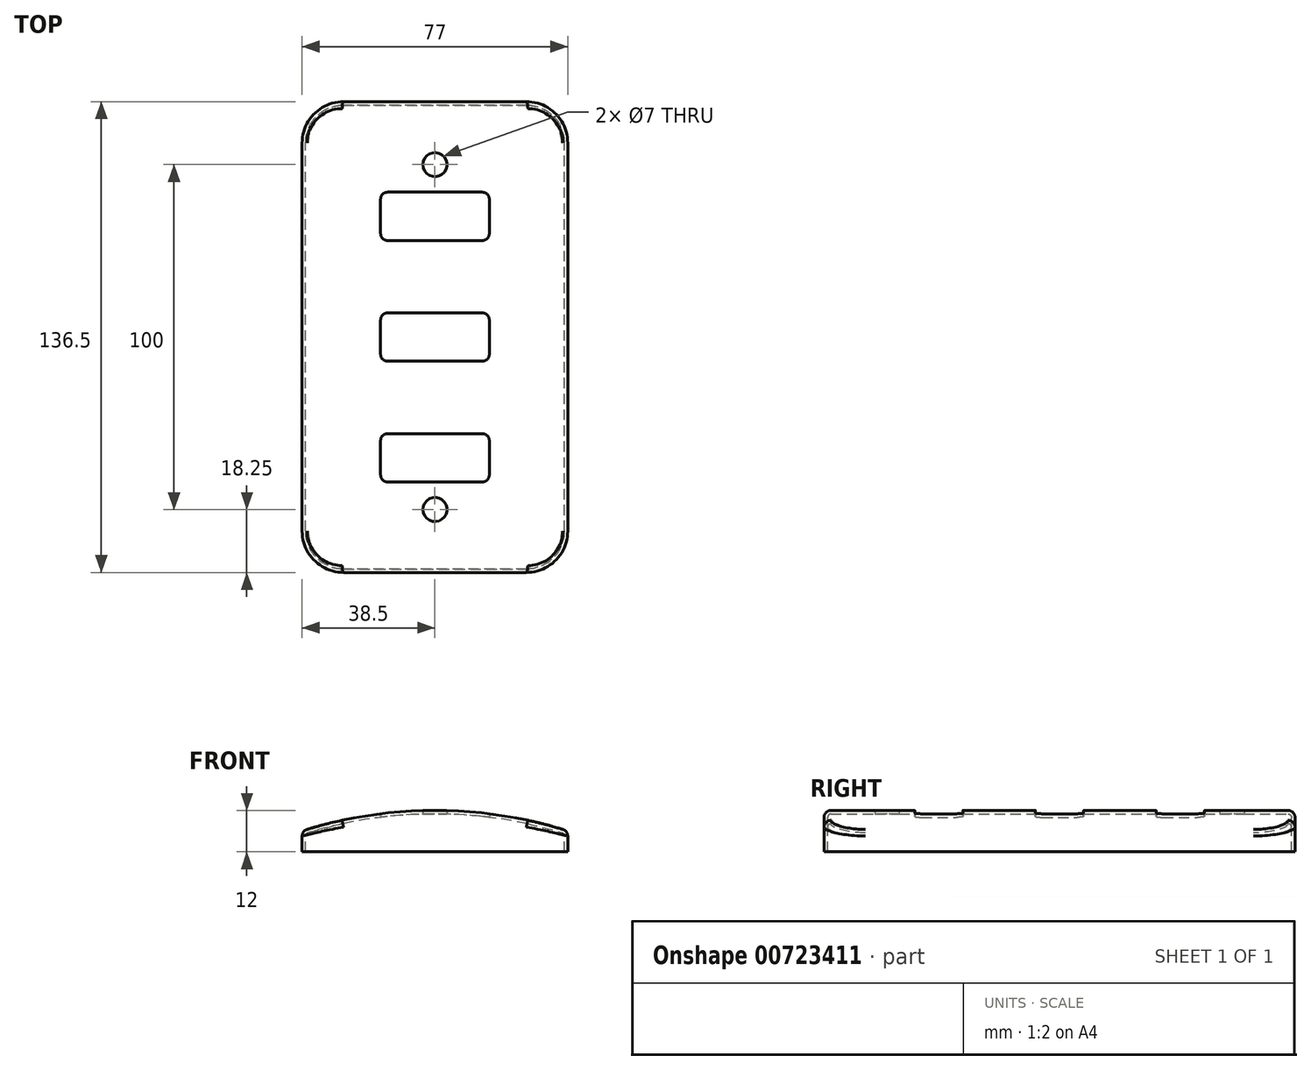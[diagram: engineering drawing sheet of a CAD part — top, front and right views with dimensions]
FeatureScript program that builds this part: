
annotation { "Feature Type Name" : "Feature", "Feature Type Description" : "" }
export const myFeature = defineFeature(function(context is Context, id is Id, definition is map)
    precondition{}
    {
        {
            var Q0;
            Q0=qCreatedBy(makeId("Front.planeOp"),FACE);
            var sketch = newSketch(context, id + "F0", { "sketchPlane" : qUnion([Q0])});
            skLineSegment(sketch, "E0.bottom", {"start": v(-38.5, 0) * mm, "end": v(38.5, 0) * mm});
            skLineSegment(sketch, "E0.left", {"start": v(-38.5, 0) * mm, "end": v(-38.5, 6.07) * mm});
            skLineSegment(sketch, "E0.right", {"start": v(38.5, 0) * mm, "end": v(38.5, 6.07) * mm});
            skArc(sketch, "E1", {"start": v(38.5, 6.07) * mm, "mid": v(0, 12) * mm, "end": v(-38.5, 6.07) * mm});
            skLineSegment(sketch, "E2", {"start": v(0, 0) * mm, "end": v(0, 12) * mm, "construction": true});
            skSolve(sketch);
        }
        {
            var Q0;
            Q0=makeQuery(id+"F0.imprint","IMPRINT",FACE,{"disambiguationData":[TD([[makeQuery(id+"F0.imprint","IMPRINT",EDGE,{"derivedFrom":sQuery(id+"F0.wireOp",EDGE,"E0.bottom")}),1.0]])]});
            extrude(context, id + "F1", {"entities" : qUnion([Q0]), "depth" : 136.5 * mm, "offsetDistance" : 25 * mm});
        }
        {
            var Q0;
            Q0=makeQuery(id+"F1.opExtrude","CAP_EDGE",EDGE,{"disambiguationData":[OSD([sQuery(id+"F0.wireOp",EDGE,"E0.right")])],"isStart":false});
            var Q1;
            Q1=makeQuery(id+"F1.opExtrude","CAP_EDGE",EDGE,{"disambiguationData":[OSD([sQuery(id+"F0.wireOp",EDGE,"E0.left")])],"isStart":false});
            var Q2;
            Q2=makeQuery(id+"F1.opExtrude","CAP_EDGE",EDGE,{"disambiguationData":[OSD([sQuery(id+"F0.wireOp",EDGE,"E0.right")])],"isStart":true});
            var Q3;
            Q3=makeQuery(id+"F1.opExtrude","CAP_EDGE",EDGE,{"disambiguationData":[OSD([sQuery(id+"F0.wireOp",EDGE,"E0.left")])],"isStart":true});
            fillet(context, id + "F2", {"entities" : qUnion([Q0, Q1, Q2, Q3]), "radius" : 12 * mm, "tangentPropagation" : true, "allowEdgeOverflow" : false});
        }
        {
            var Q0;
            Q0=makeQuery(id+"F1.opExtrude","SWEPT_FACE",FACE,{"disambiguationData":[OSD([sQuery(id+"F0.wireOp",EDGE,"E1")])]});
            fillet(context, id + "F3", {"entities" : qUnion([Q0]), "radius" : 2 * mm, "tangentPropagation" : true, "allowEdgeOverflow" : false});
        }
        {
            var Q0;
            Q0=makeQuery(id+"F1.opExtrude","SWEPT_FACE",FACE,{"disambiguationData":[OSD([sQuery(id+"F0.wireOp",EDGE,"E0.bottom")])]});
            shell(context, id + "F4", {"entities" : qUnion([Q0]), "thickness" : 1.02 * mm});
        }
        {
            var Q0;
            Q0=qCreatedBy(makeId("Top.planeOp"),FACE);
            var sketch = newSketch(context, id + "F5", { "sketchPlane" : qUnion([Q0])});
            skCircle(sketch, "E3", {"center": v(0, -18.25) * mm, "radius": 3.5 * mm});
            skCircle(sketch, "E4", {"center": v(0, -118.25) * mm, "radius": 3.5 * mm});
            skLineSegment(sketch, "E5.bottom", {"start": v(-15.75, -40.25) * mm, "end": v(15.75, -40.25) * mm});
            skLineSegment(sketch, "E5.top", {"start": v(-15.75, -26.25) * mm, "end": v(15.75, -26.25) * mm});
            skLineSegment(sketch, "E5.left", {"start": v(-15.75, -40.25) * mm, "end": v(-15.75, -26.25) * mm});
            skLineSegment(sketch, "E5.right", {"start": v(15.75, -40.25) * mm, "end": v(15.75, -26.25) * mm});
            skPoint(sketch, "E5.middle", {"position": v(0, -33.25) * mm});
            skLineSegment(sketch, "E6.bottom", {"start": v(-15.75, -75.25) * mm, "end": v(15.75, -75.25) * mm});
            skLineSegment(sketch, "E6.top", {"start": v(-15.75, -61.25) * mm, "end": v(15.75, -61.25) * mm});
            skLineSegment(sketch, "E6.left", {"start": v(-15.75, -75.25) * mm, "end": v(-15.75, -61.25) * mm});
            skLineSegment(sketch, "E6.right", {"start": v(15.75, -75.25) * mm, "end": v(15.75, -61.25) * mm});
            skPoint(sketch, "E6.middle", {"position": v(0, -68.25) * mm});
            skLineSegment(sketch, "E7.bottom", {"start": v(-15.75, -110.25) * mm, "end": v(15.75, -110.25) * mm});
            skLineSegment(sketch, "E7.top", {"start": v(-15.75, -96.25) * mm, "end": v(15.75, -96.25) * mm});
            skLineSegment(sketch, "E7.left", {"start": v(-15.75, -110.25) * mm, "end": v(-15.75, -96.25) * mm});
            skLineSegment(sketch, "E7.right", {"start": v(15.75, -110.25) * mm, "end": v(15.75, -96.25) * mm});
            skPoint(sketch, "E7.middle", {"position": v(0, -103.25) * mm});
            skPoint(sketch, "E8.0", {"position": v(38.5, -68.25) * mm});
            skSolve(sketch);
        }
        {
            var Q0;
            Q0=makeQuery(id+"F5.imprint","IMPRINT",FACE,{"disambiguationData":[TD([[makeQuery(id+"F5.imprint","IMPRINT",EDGE,{"derivedFrom":sQuery(id+"F5.wireOp",EDGE,"E4")}),1.0]])]});
            var Q1;
            Q1=makeQuery(id+"F5.imprint","IMPRINT",FACE,{"disambiguationData":[TD([[makeQuery(id+"F5.imprint","IMPRINT",EDGE,{"derivedFrom":sQuery(id+"F5.wireOp",EDGE,"E7.bottom")}),1.0]])]});
            var Q2;
            Q2=makeQuery(id+"F5.imprint","IMPRINT",FACE,{"disambiguationData":[TD([[makeQuery(id+"F5.imprint","IMPRINT",EDGE,{"derivedFrom":sQuery(id+"F5.wireOp",EDGE,"E6.bottom")}),1.0]])]});
            var Q3;
            Q3=makeQuery(id+"F5.imprint","IMPRINT",FACE,{"disambiguationData":[TD([[makeQuery(id+"F5.imprint","IMPRINT",EDGE,{"derivedFrom":sQuery(id+"F5.wireOp",EDGE,"E5.bottom")}),1.0]])]});
            var Q4;
            Q4=makeQuery(id+"F5.imprint","IMPRINT",FACE,{"disambiguationData":[TD([[makeQuery(id+"F5.imprint","IMPRINT",EDGE,{"derivedFrom":sQuery(id+"F5.wireOp",EDGE,"E3")}),1.0]])]});
            extrude(context, id + "F6", {"entities" : qUnion([Q0, Q1, Q2, Q3, Q4]), "operationType" : NewBodyOperationType.REMOVE, "endBound" : BoundingType.THROUGH_ALL, "depth" : 25 * mm, "offsetDistance" : 25 * mm});
        }
        {
            var Q0;
            Q0=makeQuery(id+"F6.boolean.opBoolean","COPY",EDGE,{"derivedFrom":makeQuery(id+"F6.opExtrude","SWEPT_EDGE",EDGE,{"disambiguationData":[OSD([sQuery(id+"F5.wireOp",EDGE,"E5.top"),sQuery(id+"F5.wireOp",EDGE,"E5.left")])]})});
            var Q1;
            Q1=makeQuery(id+"F6.boolean.opBoolean","COPY",EDGE,{"derivedFrom":makeQuery(id+"F6.opExtrude","SWEPT_EDGE",EDGE,{"disambiguationData":[OSD([sQuery(id+"F5.wireOp",EDGE,"E5.top"),sQuery(id+"F5.wireOp",EDGE,"E5.right")])]})});
            var Q2;
            Q2=makeQuery(id+"F6.boolean.opBoolean","COPY",EDGE,{"derivedFrom":makeQuery(id+"F6.opExtrude","SWEPT_EDGE",EDGE,{"disambiguationData":[OSD([sQuery(id+"F5.wireOp",EDGE,"E5.bottom"),sQuery(id+"F5.wireOp",EDGE,"E5.left")])]})});
            var Q3;
            Q3=makeQuery(id+"F6.boolean.opBoolean","COPY",EDGE,{"derivedFrom":makeQuery(id+"F6.opExtrude","SWEPT_EDGE",EDGE,{"disambiguationData":[OSD([sQuery(id+"F5.wireOp",EDGE,"E5.bottom"),sQuery(id+"F5.wireOp",EDGE,"E5.right")])]})});
            var Q4;
            Q4=makeQuery(id+"F6.boolean.opBoolean","COPY",EDGE,{"derivedFrom":makeQuery(id+"F6.opExtrude","SWEPT_EDGE",EDGE,{"disambiguationData":[OSD([sQuery(id+"F5.wireOp",EDGE,"E6.bottom"),sQuery(id+"F5.wireOp",EDGE,"E6.right")])]})});
            var Q5;
            Q5=makeQuery(id+"F6.boolean.opBoolean","COPY",EDGE,{"derivedFrom":makeQuery(id+"F6.opExtrude","SWEPT_EDGE",EDGE,{"disambiguationData":[OSD([sQuery(id+"F5.wireOp",EDGE,"E7.bottom"),sQuery(id+"F5.wireOp",EDGE,"E7.right")])]})});
            var Q6;
            Q6=makeQuery(id+"F6.boolean.opBoolean","COPY",EDGE,{"derivedFrom":makeQuery(id+"F6.opExtrude","SWEPT_EDGE",EDGE,{"disambiguationData":[OSD([sQuery(id+"F5.wireOp",EDGE,"E7.bottom"),sQuery(id+"F5.wireOp",EDGE,"E7.left")])]})});
            var Q7;
            Q7=makeQuery(id+"F6.boolean.opBoolean","COPY",EDGE,{"derivedFrom":makeQuery(id+"F6.opExtrude","SWEPT_EDGE",EDGE,{"disambiguationData":[OSD([sQuery(id+"F5.wireOp",EDGE,"E6.bottom"),sQuery(id+"F5.wireOp",EDGE,"E6.left")])]})});
            var Q8;
            Q8=makeQuery(id+"F6.boolean.opBoolean","COPY",EDGE,{"derivedFrom":makeQuery(id+"F6.opExtrude","SWEPT_EDGE",EDGE,{"disambiguationData":[OSD([sQuery(id+"F5.wireOp",EDGE,"E6.top"),sQuery(id+"F5.wireOp",EDGE,"E6.left")])]})});
            var Q9;
            Q9=makeQuery(id+"F6.boolean.opBoolean","COPY",EDGE,{"derivedFrom":makeQuery(id+"F6.opExtrude","SWEPT_EDGE",EDGE,{"disambiguationData":[OSD([sQuery(id+"F5.wireOp",EDGE,"E7.top"),sQuery(id+"F5.wireOp",EDGE,"E7.left")])]})});
            var Q10;
            Q10=makeQuery(id+"F6.boolean.opBoolean","COPY",EDGE,{"derivedFrom":makeQuery(id+"F6.opExtrude","SWEPT_EDGE",EDGE,{"disambiguationData":[OSD([sQuery(id+"F5.wireOp",EDGE,"E6.top"),sQuery(id+"F5.wireOp",EDGE,"E6.right")])]})});
            var Q11;
            Q11=makeQuery(id+"F6.boolean.opBoolean","COPY",EDGE,{"derivedFrom":makeQuery(id+"F6.opExtrude","SWEPT_EDGE",EDGE,{"disambiguationData":[OSD([sQuery(id+"F5.wireOp",EDGE,"E7.top"),sQuery(id+"F5.wireOp",EDGE,"E7.right")])]})});
            fillet(context, id + "F7", {"entities" : qUnion([Q0, Q1, Q2, Q3, Q4, Q5, Q6, Q7, Q8, Q9, Q10, Q11]), "radius" : 2 * mm, "tangentPropagation" : true, "allowEdgeOverflow" : false});
        }
    });
